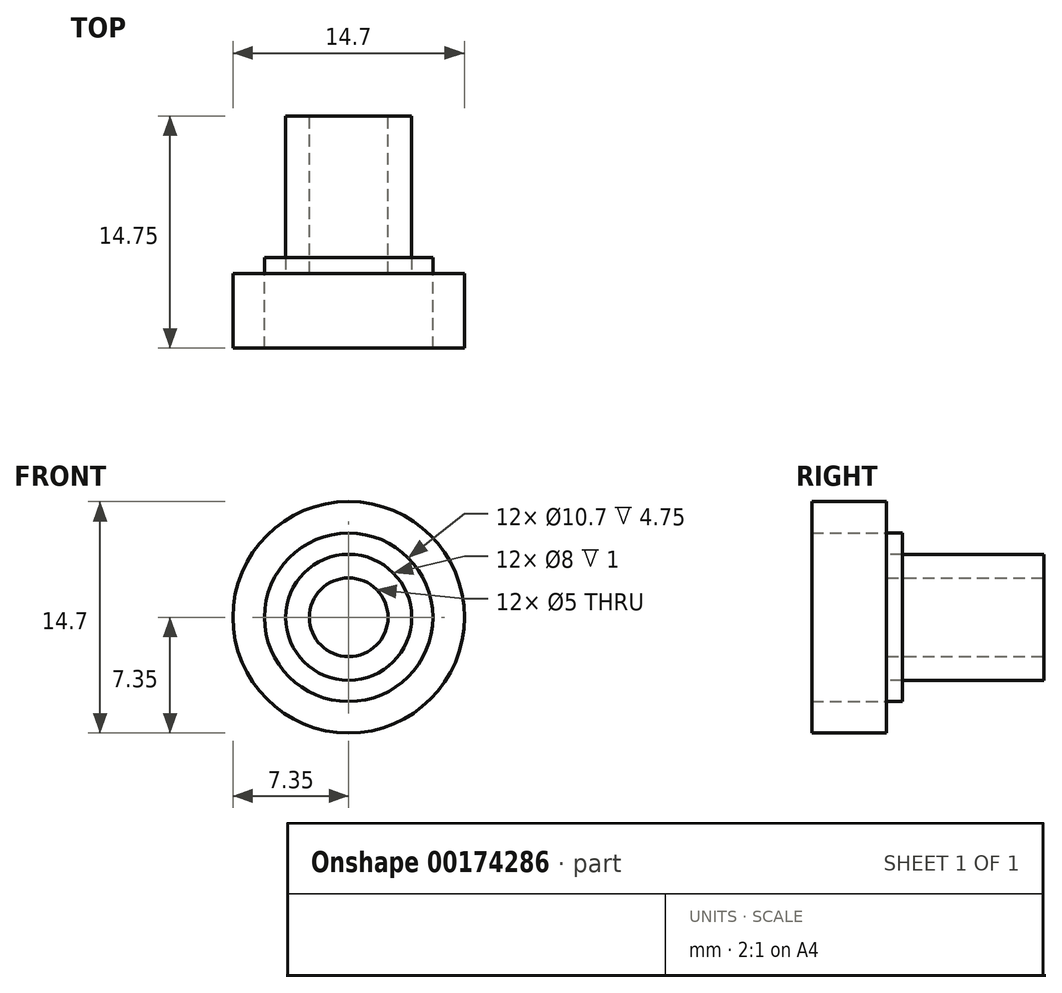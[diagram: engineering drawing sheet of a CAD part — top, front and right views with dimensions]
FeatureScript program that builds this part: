
annotation { "Feature Type Name" : "Feature", "Feature Type Description" : "" }
export const myFeature = defineFeature(function(context is Context, id is Id, definition is map)
    precondition{}
    {
        {
            var Q0;
            Q0=qCreatedBy(makeId("Front.planeOp"),FACE);
            var sketch = newSketch(context, id + "F0", { "sketchPlane" : qUnion([Q0])});
            skCircle(sketch, "E0", {"center": v(0, 0) * mm, "radius": 2.5 * mm});
            skCircle(sketch, "E1", {"center": v(0, 0) * mm, "radius": 4 * mm});
            skCircle(sketch, "E2", {"center": v(0, 0) * mm, "radius": 5.35 * mm});
            skSolve(sketch);
        }
        {
            var Q0;
            Q0=makeQuery(id+"F0.imprint","IMPRINT",FACE,{"disambiguationData":[TD([[makeQuery(id+"F0.imprint","IMPRINT",EDGE,{"derivedFrom":sQuery(id+"F0.wireOp",EDGE,"E0")}),-1.0]])]});
            extrude(context, id + "F1", {"entities" : qUnion([Q0]), "depth" : 10 * mm});
        }
        {
            var Q0;
            Q0=makeQuery(id+"F1.opExtrude","CAP_FACE",FACE,{"disambiguationData":[OSD([sQuery(id+"F0.wireOp",EDGE,"E0"),sQuery(id+"F0.wireOp",EDGE,"E1")])],"isStart":false});
            var sketch = newSketch(context, id + "F2", { "sketchPlane" : qUnion([Q0])});
            skCircle(sketch, "E3", {"center": v(0, 0) * mm, "radius": 5.35 * mm});
            skCircle(sketch, "E4.0", {"center": v(0, 0) * mm, "radius": 7.35 * mm});
            skSolve(sketch);
        }
        {
            var Q0;
            Q0=makeQuery(id+"F2.imprint","IMPRINT",FACE,{"disambiguationData":[TD([[makeQuery(id+"F2.imprint","IMPRINT",EDGE,{"derivedFrom":sQuery(id+"F2.wireOp",EDGE,"E3")}),-1.0]])]});
            extrude(context, id + "F3", {"entities" : qUnion([Q0]), "depth" : 4.75 * mm});
        }
        {
            var Q0;
            Q0=makeQuery(id+"F2.imprint","IMPRINT",FACE,{"disambiguationData":[TD([[makeQuery(id+"F2.imprint","IMPRINT",EDGE,{"derivedFrom":sQuery(id+"F2.wireOp",EDGE,"E3")}),1.0]])]});
            extrude(context, id + "F4", {"entities" : qUnion([Q0]), "oppositeDirection" : true, "depth" : 1 * mm});
        }
    });
